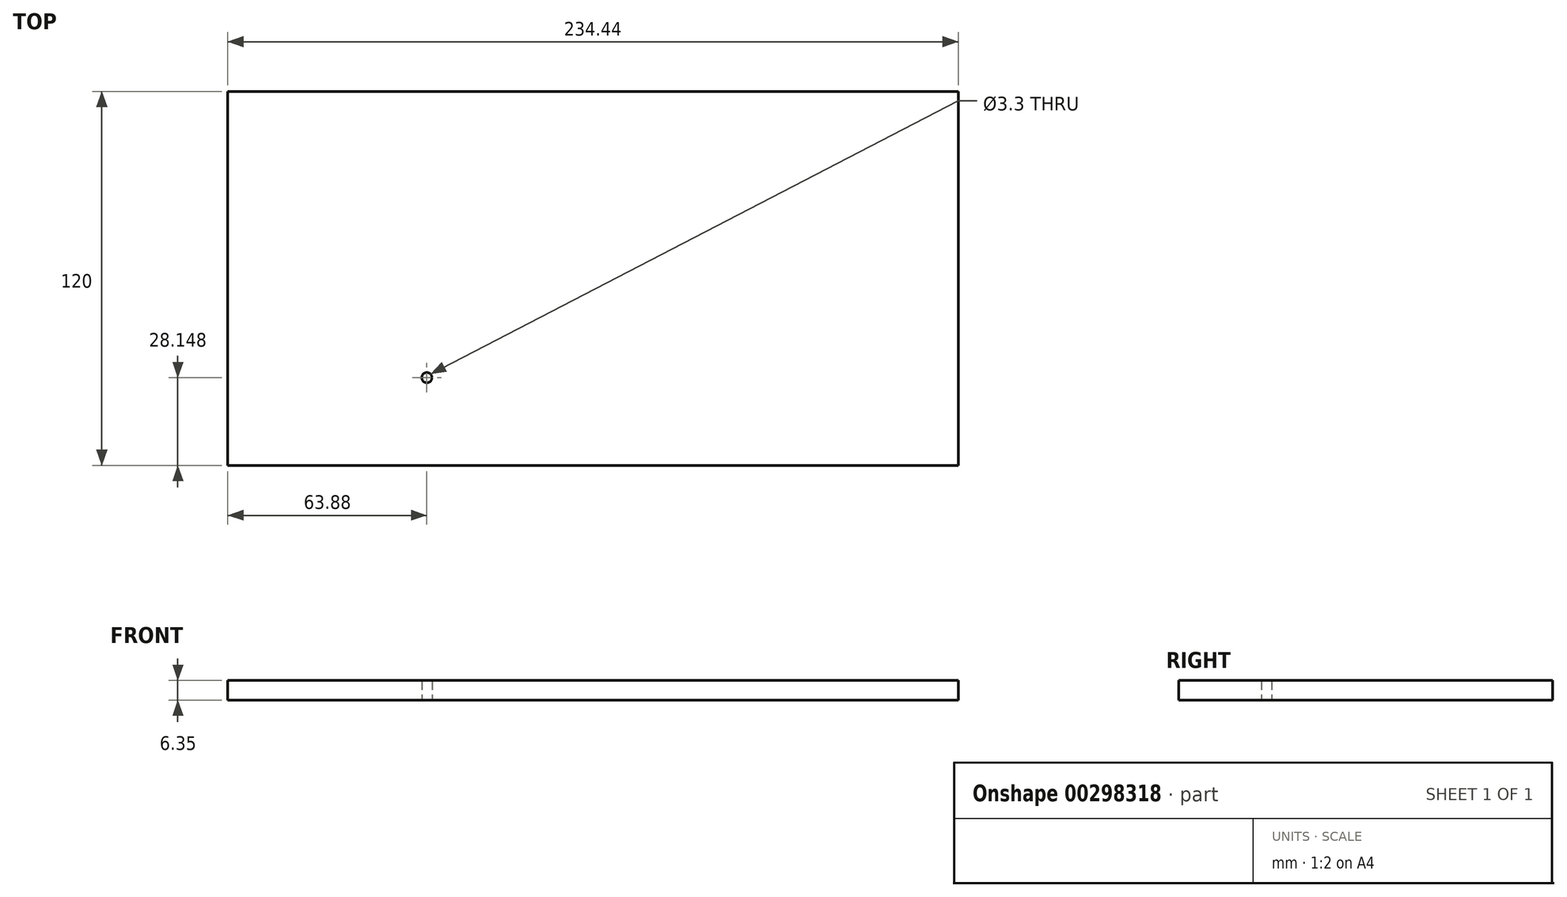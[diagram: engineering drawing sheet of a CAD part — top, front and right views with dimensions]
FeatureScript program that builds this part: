
annotation { "Feature Type Name" : "Feature", "Feature Type Description" : "" }
export const myFeature = defineFeature(function(context is Context, id is Id, definition is map)
    precondition{}
    {
        {
            var Q0;
            Q0=qCreatedBy(makeId("Top.planeOp"),FACE);
            var sketch = newSketch(context, id + "F0", { "sketchPlane" : qUnion([Q0])});
            skLineSegment(sketch, "E0.bottom", {"start": v(117.22, -60) * mm, "end": v(-117.22, -60) * mm});
            skLineSegment(sketch, "E0.top", {"start": v(117.22, 60) * mm, "end": v(-117.22, 60) * mm});
            skLineSegment(sketch, "E0.left", {"start": v(117.22, -60) * mm, "end": v(117.22, 60) * mm});
            skLineSegment(sketch, "E0.right", {"start": v(-117.22, -60) * mm, "end": v(-117.22, 60) * mm});
            skPoint(sketch, "E0.middle", {"position": v(0, 0) * mm});
            skPoint(sketch, "E1", {"position": v(-53.34, -31.85) * mm});
            skPoint(sketch, "E2", {"position": v(62.48, 33.38) * mm});
            skSolve(sketch);
        }
        {
            var Q0;
            Q0=makeQuery(id+"F0.imprint","IMPRINT",FACE,{"disambiguationData":[TD([[makeQuery(id+"F0.imprint","IMPRINT",EDGE,{"derivedFrom":sQuery(id+"F0.wireOp",EDGE,"E0.bottom")}),-1.0]])]});
            extrude(context, id + "F1", {"entities" : qUnion([Q0]), "depth" : 6.35 * mm});
        }
        {
            var Q0;
            Q0=sQuery(id+"F0.wireOp",VERTEX,"E1");
            var Q1;
            Q1=makeQuery(id+"F1.opExtrude","SWEPT_BODY",BODY,{"disambiguationData":[OSD([sQuery(id+"F0.wireOp",EDGE,"E0.bottom"),sQuery(id+"F0.wireOp",EDGE,"E0.top"),sQuery(id+"F0.wireOp",EDGE,"E0.left"),sQuery(id+"F0.wireOp",EDGE,"E0.right")])]});
            hole(context, id + "F2", {"style" : HoleStyle.SIMPLE, "endStyle" : HoleEndStyle.BLIND, "oppositeDirection" : true, "standardTappedOrClearance" : lookupTablePath({ "standard" : "ISO", "engagement" : "75%", "pitch" : "0.7 mm", "size" : "M4", "type" : "Tapped" }), "standardBlindInLast" : lookupTablePath({ "standard" : "ISO", "engagement" : "75%", "pitch" : "0.7 mm", "size" : "M4", "type" : "Tapped" }), "holeDiameter" : 3.3 * mm, "showTappedDepth" : true, "holeDepth" : 20.35 * mm, "tappedDepth" : 6.35 * mm, "tapClearance" : 20, "locations" : qUnion([Q0]), "scope" : qUnion([Q1]), "majorDiameter" : 4 * mm});
        }
    });
